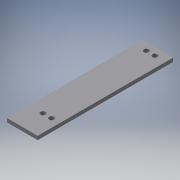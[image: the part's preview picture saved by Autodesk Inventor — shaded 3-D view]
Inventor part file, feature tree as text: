
AUTODESK INVENTOR PART (.ipt)
format: ipt  version: 2016 (Build 200138000, 138)  size: 103,936 bytes
history: native  units: mm
features: reference x6, extrude x3, sketch x3
ambient origin geometry x8: Origin, YZ Plane, XZ Plane, XY Plane, X Axis, Y Axis, Z Axis, Center Point
bodies: Solid1 (feature_tree)
feature tree (12):
  extrude  "Extrusion1"  Depth=220.0mm
  extrude  "Extrusion2"  TaperAngle=0.0deg  [1 undecoded]
  extrude  "Extrusion3"  [1 undecoded]
  sketch  "Sketch1"  dims[d0=50.0mm d1=220.0mm]
  sketch  "Sketch2"  dims[d2=6.0mm d3=0.0mm d4=0.0mm d5=0.0mm]
  reference  "Reference1"
  reference  "Reference2"
  reference  "Reference3"
  reference  "Reference4"
  sketch  "Sketch3"  dims[d6=6.0mm d7=0.0mm]
  reference  "Reference5"
  reference  "Reference6"
note: 2 required parameter values undecoded (feature->parameter linkage not recoverable at this tier; creation-order binding heuristic only, values carry confidence <= 0.55)
